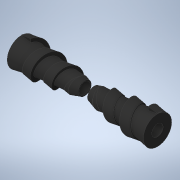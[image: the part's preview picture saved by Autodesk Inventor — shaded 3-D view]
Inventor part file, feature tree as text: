
AUTODESK INVENTOR PART (.ipt)
format: ipt  version: 2022 (Build 260153000, 153)  size: 460,288 bytes
history: native  units: mm
features: sketch x9, extrude x5, revolve x3, mirror x2, projected_geometry x2, other x1, helix x1
ambient origin geometry x8: Origin, YZ Plane, XZ Plane, XY Plane, X Axis, Y Axis, Z Axis, Center Point
bodies: Volumenkörper1 (feature_tree), Solid2 (feature_tree), Solid3 (feature_tree)
feature tree (23):
  extrude  "Extrusion1"  Depth=11.0mm
  other  "Spirale1"
  mirror  "Spiegeln1"
  extrude  "Extrusion5"  Depth=10.0mm
  extrude  "Extrusion6"  Depth=1.0mm
  sketch  "Sketch9"  dims[d19=0.1mm d32=10.0mm d33=0.0mm]
  revolve  "Revolution1"  [1 undecoded]
  revolve  "Revolution2"  [1 undecoded]
  helix  "Coil2"  [1 undecoded]
  mirror  "Mirror2"
  extrude  "Extrusion7"  Depth=2.0mm
  extrude  "Extrusion8"  TaperAngle=90.0deg  [1 undecoded]
  revolve  "Revolution3"  [1 undecoded]
  sketch  "Skizze1"  dims[d0=6.0mm d1=11.0mm]
  sketch  "Skizze3"  dims[d2=36.0mm d3=0.0mm]
  projected_geometry  "Projizierte Kontur2"
  sketch  "Sketch7"  dims[d8=7.0mm d9=24.5mm d10=10.0mm d11=0.0mm d12=90.0deg d13=90.0deg d14=0.0mm d15=0.0mm d16=4.0mm]
  sketch  "Sketch8"  dims[d17=13.962634mm d18=1.0mm]
  projected_geometry  "Projected Loop4"
  sketch  "Sketch10"  dims[d34=7.0mm d35=100.0mm d36=0.0mm d37=82.0mm d38=0.0mm]
  sketch  "Sketch11"  dims[d41=2.0mm d42=2.0mm]
  sketch  "Sketch12"  dims[d43=200.0mm d44=90.0deg]
  sketch  "Sketch13"  dims[d45=90.0deg d47=0.0mm d48=13.962634mm d49=5.0mm d50=2.2mm d51=0.6mm d53=10.0mm d54=10.0mm d55=30.0mm d56=-1.204277mm d57=90.0deg d58=90.0deg d59=0.0mm d60=0.0mm d61=13.962634mm d62=7.1mm d63=80.0mm d64=0.0mm d65=15.0mm d66=5.0mm d67=0.0mm d68=3.5mm d69=3.5mm d70=360.0deg d71=1.0mm d72=0.0mm]
note: 5 required parameter values undecoded (feature->parameter linkage not recoverable at this tier; creation-order binding heuristic only, values carry confidence <= 0.55)